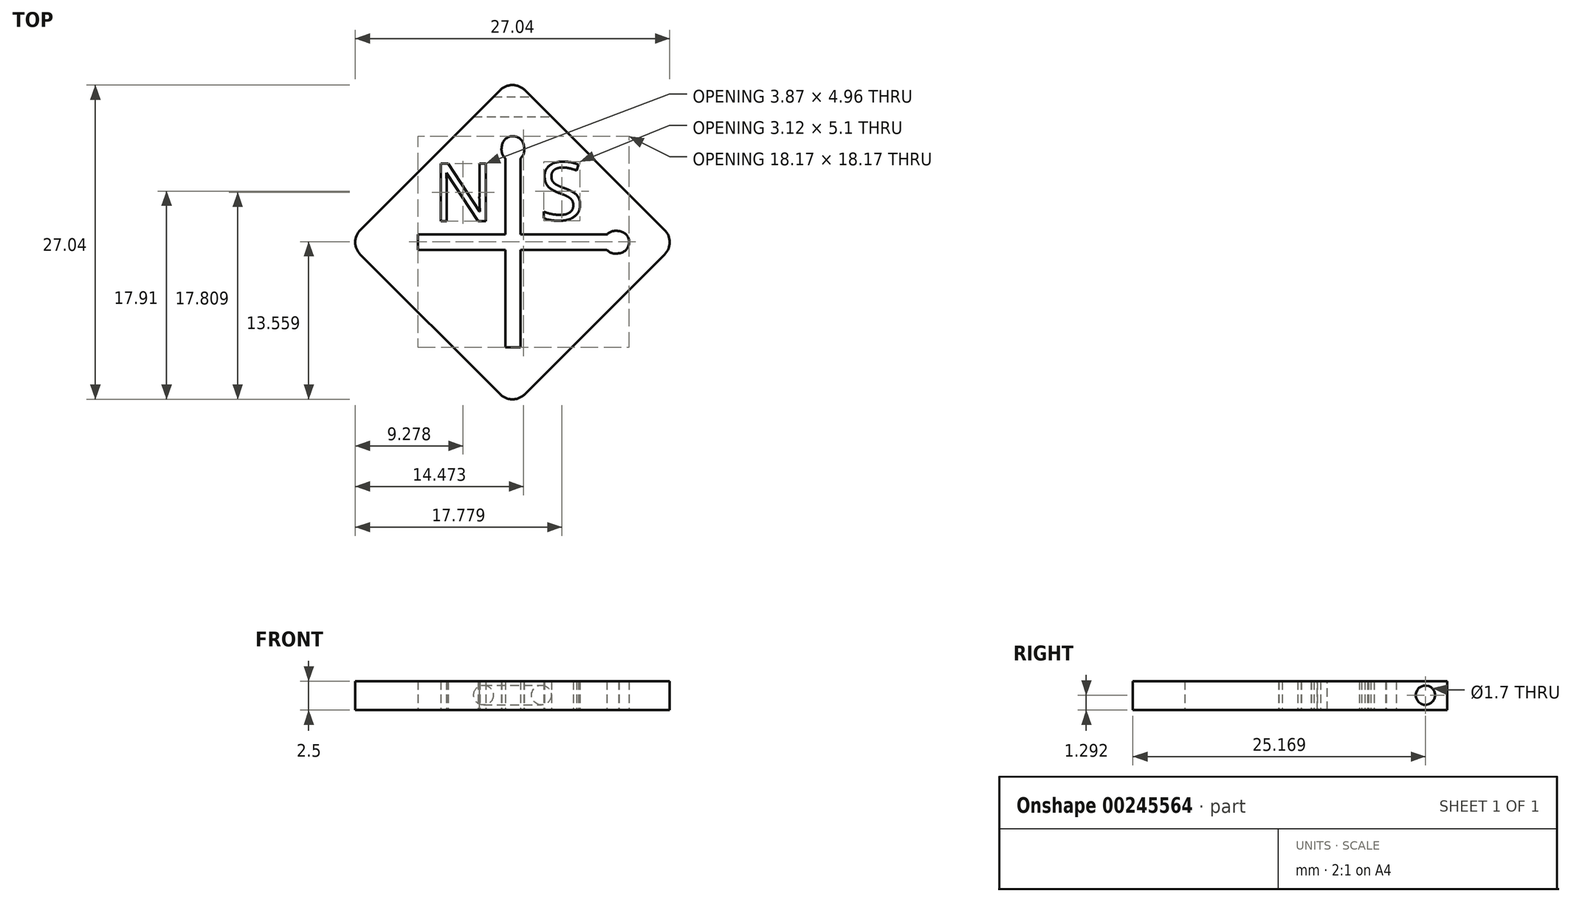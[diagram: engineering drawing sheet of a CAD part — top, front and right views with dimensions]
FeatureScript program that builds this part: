
annotation { "Feature Type Name" : "Feature", "Feature Type Description" : "" }
export const myFeature = defineFeature(function(context is Context, id is Id, definition is map)
    precondition{}
    {
        {
            var Q0;
            Q0=qCreatedBy(makeId("Top.planeOp"),FACE);
            var sketch = newSketch(context, id + "F0", { "sketchPlane" : qUnion([Q0])});
            skLineSegment(sketch, "E0", {"start": v(1.06, -1.06) * mm, "end": v(13.08, -13.08) * mm});
            skLineSegment(sketch, "E1", {"start": v(13.08, -15.2) * mm, "end": v(1.06, -27.22) * mm});
            skLineSegment(sketch, "E2", {"start": v(-1.06, -27.22) * mm, "end": v(-13.08, -15.2) * mm});
            skLineSegment(sketch, "E3", {"start": v(-13.08, -13.08) * mm, "end": v(-1.06, -1.06) * mm});
            skPoint(sketch, "E4.visualSharp", {"position": v(0, 0) * mm});
            skArc(sketch, "E4.filletArc", {"start": v(1.06, -1.06) * mm, "mid": v(0, -0.62) * mm, "end": v(-1.06, -1.06) * mm});
            skPoint(sketch, "E5.visualSharp", {"position": v(-14.14, -14.14) * mm});
            skArc(sketch, "E5.filletArc", {"start": v(-13.08, -13.08) * mm, "mid": v(-13.52, -14.14) * mm, "end": v(-13.08, -15.2) * mm});
            skPoint(sketch, "E6.visualSharp", {"position": v(14.14, -14.14) * mm});
            skArc(sketch, "E6.filletArc", {"start": v(13.08, -15.2) * mm, "mid": v(13.52, -14.14) * mm, "end": v(13.08, -13.08) * mm});
            skPoint(sketch, "E7.visualSharp", {"position": v(0, -28.28) * mm});
            skArc(sketch, "E7.filletArc", {"start": v(-1.06, -27.22) * mm, "mid": v(0, -27.66) * mm, "end": v(1.06, -27.22) * mm});
            skLineSegment(sketch, "E8", {"start": v(0, 0) * mm, "end": v(0, -31.86) * mm, "construction": true});
            skLineSegment(sketch, "E9", {"start": v(-14.14, -14.14) * mm, "end": v(14.14, -14.14) * mm, "construction": true});
            skLineSegment(sketch, "E10", {"start": v(-8.13, -13.48) * mm, "end": v(-8.13, -14.8) * mm});
            skLineSegment(sketch, "E11", {"start": v(-8.13, -14.8) * mm, "end": v(8.13, -14.8) * mm});
            skLineSegment(sketch, "E12", {"start": v(8.13, -13.48) * mm, "end": v(-8.13, -13.48) * mm});
            skLineSegment(sketch, "E13", {"start": v(-8.13, -13.48) * mm, "end": v(0, -13.48) * mm, "construction": true});
            skLineSegment(sketch, "E14", {"start": v(0, -13.48) * mm, "end": v(8.13, -13.48) * mm, "construction": true});
            skArc(sketch, "E15", {"start": v(9.18, -15.1) * mm, "mid": v(10.04, -14.12) * mm, "end": v(9.13, -13.2) * mm});
            skArc(sketch, "E16", {"start": v(9.13, -13.2) * mm, "mid": v(8.6, -13.2) * mm, "end": v(8.13, -13.48) * mm});
            skArc(sketch, "E17", {"start": v(8.13, -14.8) * mm, "mid": v(8.61, -15.1) * mm, "end": v(9.18, -15.1) * mm});
            skLineSegment(sketch, "E18", {"start": v(-0.62, -23.19) * mm, "end": v(0.7, -23.19) * mm});
            skLineSegment(sketch, "E19", {"start": v(0.7, -23.19) * mm, "end": v(0.7, -6.92) * mm});
            skLineSegment(sketch, "E20", {"start": v(-0.62, -6.92) * mm, "end": v(-0.62, -23.19) * mm});
            skLineSegment(sketch, "E21", {"start": v(-0.62, -23.19) * mm, "end": v(-0.62, -15.05) * mm, "construction": true});
            skLineSegment(sketch, "E22", {"start": v(-0.62, -15.05) * mm, "end": v(-0.62, -6.92) * mm, "construction": true});
            skArc(sketch, "E23", {"start": v(0.99, -5.88) * mm, "mid": v(0.02, -5.01) * mm, "end": v(-0.91, -5.92) * mm});
            skArc(sketch, "E24", {"start": v(-0.91, -5.92) * mm, "mid": v(-0.9, -6.46) * mm, "end": v(-0.62, -6.92) * mm});
            skArc(sketch, "E25", {"start": v(0.7, -6.92) * mm, "mid": v(1, -6.44) * mm, "end": v(0.99, -5.88) * mm});
            skText(sketch, "E26", { "text": "N\n", "fontName": "OpenSans-Regular.ttf"});
            skText(sketch, "E27", { "text": "S", "fontName": "OpenSans-Regular.ttf"});
            const initialGuessF0  = {"E26": [-0.00686, -0.01233, 1, 0, 0.005], "E27": [0.00234, -0.01223, 1, 0, 0.005]};
            skSetInitialGuess(sketch, initialGuessF0);
            skSolve(sketch);
        }
        {
            var Q0;
            Q0=makeQuery(id+"F0.imprint","IMPRINT",FACE,{"disambiguationData":[TD([[makeQuery(id+"F0.imprint","IMPRINT",EDGE,{"derivedFrom":sQuery(id+"F0.wireOp",EDGE,"E0")}),-1.0]])]});
            extrude(context, id + "F1", {"entities" : qUnion([Q0]), "depth" : 2.5 * mm});
        }
        {
            var Q0;
            Q0=qCreatedBy(makeId("Right.planeOp"),FACE);
            var sketch = newSketch(context, id + "F2", { "sketchPlane" : qUnion([Q0])});
            skCircle(sketch, "E28", {"center": v(-2.5, 1.3) * mm, "radius": 0.85 * mm});
            skSolve(sketch);
        }
        {
            var Q0;
            Q0=qSketchRegion(id+"F2",true);
            extrude(context, id + "F3", {"entities" : qUnion([Q0]), "operationType" : NewBodyOperationType.REMOVE, "endBound" : BoundingType.SYMMETRIC, "oppositeDirection" : true, "depth" : 25 * mm});
        }
    });
